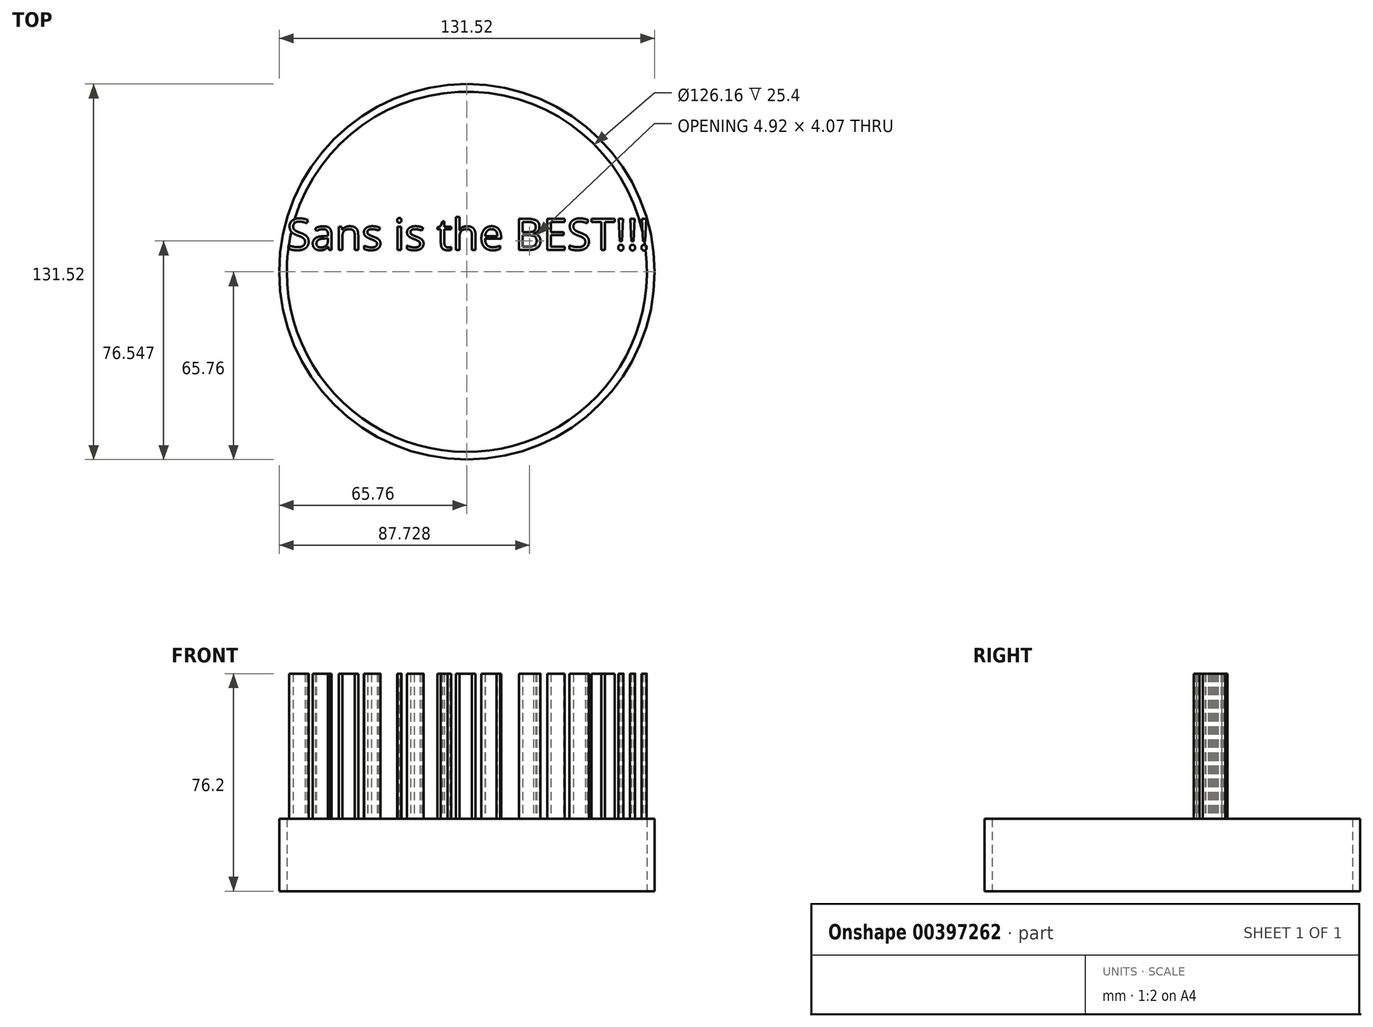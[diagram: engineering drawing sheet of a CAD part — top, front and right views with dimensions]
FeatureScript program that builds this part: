
annotation { "Feature Type Name" : "Feature", "Feature Type Description" : "" }
export const myFeature = defineFeature(function(context is Context, id is Id, definition is map)
    precondition{}
    {
        {
            var Q0;
            Q0=qCreatedBy(makeId("Top.planeOp"),FACE);
            var sketch = newSketch(context, id + "F0", { "sketchPlane" : qUnion([Q0])});
            skCircle(sketch, "E0", {"center": v(0, 0) * mm, "radius": 65.76 * mm});
            skCircle(sketch, "E1", {"center": v(0, 0) * mm, "radius": 57.94 * mm});
            skCircle(sketch, "E2", {"center": v(0, 0) * mm, "radius": 50.91 * mm});
            skCircle(sketch, "E3", {"center": v(0, 0) * mm, "radius": 43.74 * mm});
            skLineSegment(sketch, "E4", {"start": v(-31.61, 3.7) * mm, "end": v(-10.03, 3.7) * mm});
            skLineSegment(sketch, "E5", {"start": v(-10.03, 3.7) * mm, "end": v(0, 27.9) * mm});
            skLineSegment(sketch, "E6", {"start": v(0, 27.9) * mm, "end": v(11.77, 3.7) * mm});
            skLineSegment(sketch, "E7", {"start": v(11.77, 3.7) * mm, "end": v(32.7, 3.7) * mm});
            skLineSegment(sketch, "E8", {"start": v(32.7, 3.7) * mm, "end": v(11.77, -12.64) * mm});
            skLineSegment(sketch, "E9", {"start": v(11.77, -12.64) * mm, "end": v(19.62, -28.34) * mm});
            skLineSegment(sketch, "E10", {"start": v(19.62, -28.34) * mm, "end": v(0, -12.64) * mm});
            skLineSegment(sketch, "E11", {"start": v(0, -12.64) * mm, "end": v(-12.56, -28.34) * mm});
            skLineSegment(sketch, "E12", {"start": v(-12.56, -28.34) * mm, "end": v(-10.03, -12.64) * mm});
            skLineSegment(sketch, "E13", {"start": v(-10.03, -12.64) * mm, "end": v(-31.61, 3.7) * mm});
            skSolve(sketch);
        }
        {
            var Q0;
            Q0 = qSketchRegion(id + "F0", true);
            var Q1;
            Q1=makeQuery(id+"F0.imprint","IMPRINT",FACE,{"disambiguationData":[TD([[makeQuery(id+"F0.imprint","IMPRINT",EDGE,{"derivedFrom":sQuery(id+"F0.wireOp",EDGE,"E1")}),1.0]])]});
            var Q2;
            Q2=makeQuery(id+"F0.imprint","IMPRINT",FACE,{"disambiguationData":[TD([[makeQuery(id+"F0.imprint","IMPRINT",EDGE,{"derivedFrom":sQuery(id+"F0.wireOp",EDGE,"E2")}),1.0]])]});
            var Q3;
            Q3=makeQuery(id+"F0.imprint","IMPRINT",FACE,{"disambiguationData":[TD([[makeQuery(id+"F0.imprint","IMPRINT",EDGE,{"derivedFrom":sQuery(id+"F0.wireOp",EDGE,"E3")}),1.0]])]});
            var Q4;
            Q4=makeQuery(id+"F0.imprint","IMPRINT",FACE,{"disambiguationData":[TD([[makeQuery(id+"F0.imprint","IMPRINT",EDGE,{"derivedFrom":sQuery(id+"F0.wireOp",EDGE,"E4")}),-1.0]])]});
            extrude(context, id + "F1", {"entities" : qUnion([Q0, Q1, Q2, Q3, Q4]), "depth" : 25.4 * mm});
        }
        {
            var Q0;
            Q0=makeQuery(id+"F1.opExtrude","CAP_FACE",FACE,{"disambiguationData":[OSD([sQuery(id+"F0.wireOp",EDGE,"E0")])],"isStart":false});
            var sketch = newSketch(context, id + "F2", { "sketchPlane" : qUnion([Q0])});
            skText(sketch, "E14", { "text": "Sans is the BEST!!!\n", "fontName": "OpenSans-Regular.ttf"});
            const initialGuessF2  = {"E14": [-0.06306, 0.00767, 1, 0, 0.01098]};
            skSetInitialGuess(sketch, initialGuessF2);
            skSolve(sketch);
        }
        {
            var Q0;
            Q0 = qSketchRegion(id + "F2", true);
            extrude(context, id + "F3", {"entities" : qUnion([Q0]), "operationType" : NewBodyOperationType.ADD, "depth" : 50.8 * mm});
        }
        {
            var Q0;
            {var subQ0=sQuery(id+"F0.wireOp",EDGE,"E0");Q0=makeQuery(id+"F3.boolean.opBoolean","SPLIT",FACE,{"disambiguationData":[TD([makeQuery(id+"F1.opExtrude","SWEPT_FACE",FACE,{"disambiguationData":[OSD([subQ0])]})])],"derivedFrom":makeQuery(id+"F1.opExtrude","CAP_FACE",FACE,{"disambiguationData":[OSD([subQ0])],"isStart":false})});}
            var sketch = newSketch(context, id + "F4", { "sketchPlane" : qUnion([Q0])});
            skText(sketch, "E15", { "text": "-Willem G.", "fontName": "OpenSans-Regular.ttf"});
            const initialGuessF4  = {"E15": [-0.00872, -0.01417, 1, 0, 0.01003]};
            skSetInitialGuess(sketch, initialGuessF4);
            skSolve(sketch);
        }
        {
            var Q0;
            Q0 = qSketchRegion(id + "F4", true);
            extrude(context, id + "F5", {"entities" : qUnion([Q0]), "operationType" : NewBodyOperationType.REMOVE, "oppositeDirection" : true, "depth" : 25.4 * mm});
        }
        {
            var Q0;
            {var subQ0=sQuery(id+"F0.wireOp",EDGE,"E0");Q0=makeQuery(id+"F5.boolean.opBoolean","SPLIT",FACE,{"disambiguationData":[TD([makeQuery(id+"F1.opExtrude","SWEPT_FACE",FACE,{"disambiguationData":[OSD([subQ0])]})])],"derivedFrom":makeQuery(id+"F1.opExtrude","CAP_FACE",FACE,{"disambiguationData":[OSD([subQ0])],"isStart":true})});}
            var sketch = newSketch(context, id + "F6", { "sketchPlane" : qUnion([Q0])});
            skCircle(sketch, "E16", {"center": v(0, 0) * mm, "radius": 63.08 * mm});
            skSolve(sketch);
        }
        {
            var Q0;
            Q0 = qSketchRegion(id + "F6", true);
            extrude(context, id + "F7", {"entities" : qUnion([Q0]), "operationType" : NewBodyOperationType.REMOVE, "oppositeDirection" : true, "depth" : 25.4 * mm});
        }
    });
